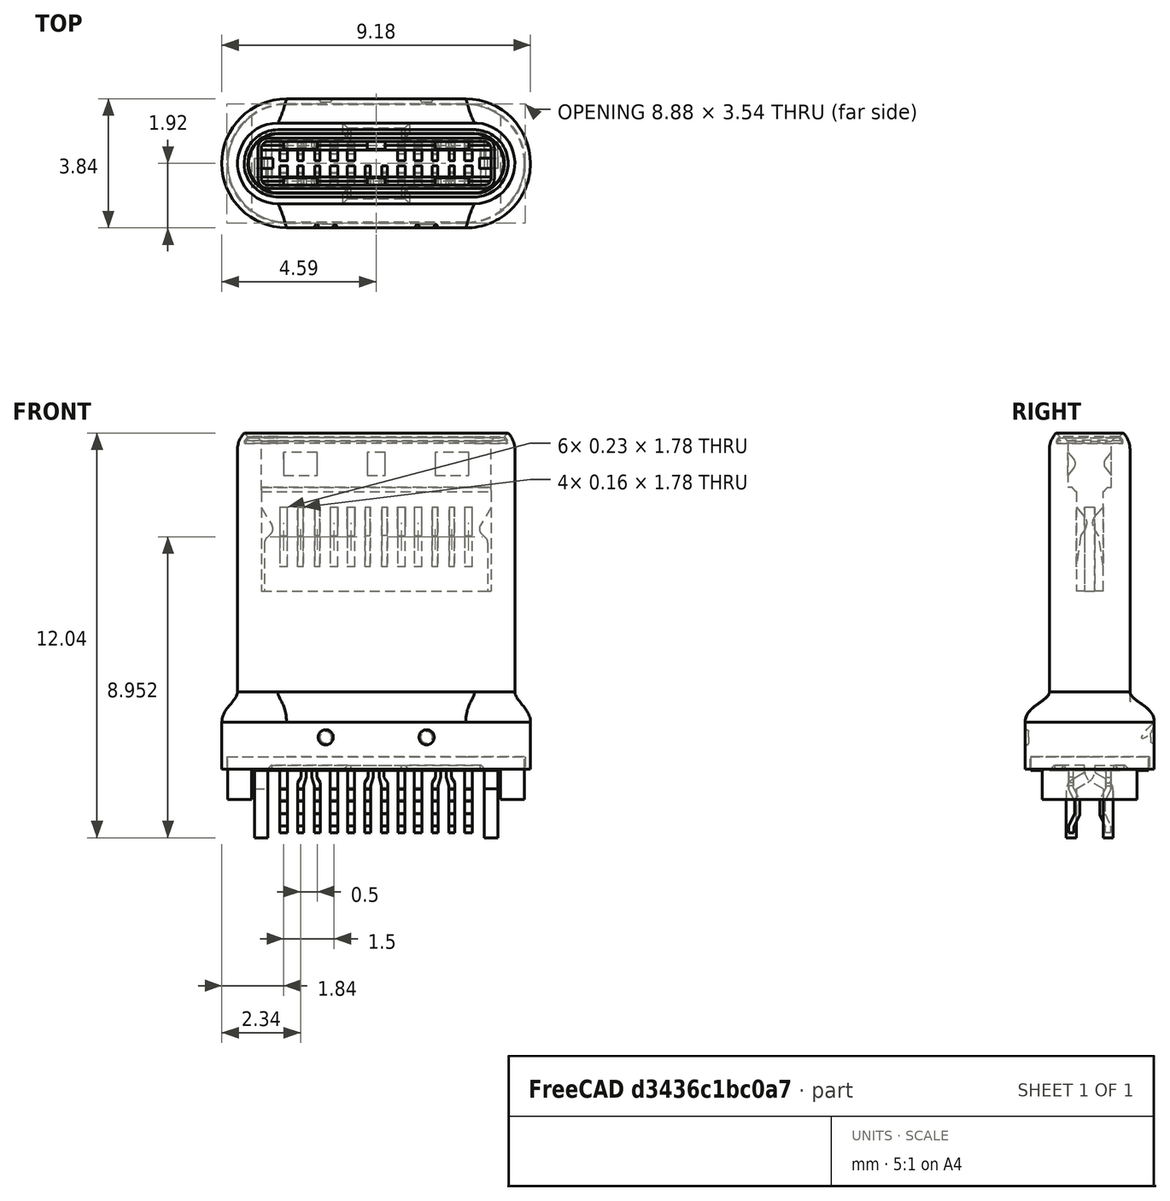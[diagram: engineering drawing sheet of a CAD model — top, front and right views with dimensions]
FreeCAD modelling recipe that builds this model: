
FCSTD DOCUMENT  (FreeCAD 0.16R6712 (Git))
Label: edges
License: All rights reserved
LicenseURL: http://en.wikipedia.org/wiki/All_rights_reserved
objects: Part::Feature×2, Sketcher::SketchObject×1
note: 3 computed .brp shape members not serialized (recipe doc carries the construction recipe); baked Part::Feature solids carry a one-line shape summary decoded from their .brp

FEATURE [Part::Feature] Part__Feature  label="SOLID"
  shape: bbox 9.212 x 3.852 x 12.05 mm, 648 faces (baked)
FEATURE [Part::Feature] Part__Feature001  label="COMPOUND"
  shape: bbox 7.54 x 0.6 x 1.955 mm, 0 faces, 0 solids (baked)
FEATURE [Sketcher::SketchObject] Sketch
  Placement = pos=(0,0,0) rot=(1,0,0;1.5708rad)
  sketch-geometry (15):
    g0: LineSegment StartX=-4.3 StartY=-7 StartZ=0 EndX=-4.3 EndY=-3.32 EndZ=0
    g1: LineSegment StartX=-4.3 StartY=-3.32 StartZ=0 EndX=-3.3 EndY=-3.32 EndZ=0
    g2: LineSegment StartX=-3.05 StartY=-3.07 StartZ=0 EndX=-3.05 EndY=-2.36 EndZ=0
    g3: LineSegment StartX=-3.05 StartY=-2.36 StartZ=0 EndX=3.05 EndY=-2.36 EndZ=0
    g4: LineSegment StartX=3.05 StartY=-2.36 StartZ=0 EndX=3.05 EndY=-3.07 EndZ=0
    g5: LineSegment StartX=3.3 StartY=-3.32 StartZ=0 EndX=4.3 EndY=-3.32 EndZ=0
    g6: LineSegment StartX=4.3 StartY=-3.32 StartZ=0 EndX=4.3 EndY=-7 EndZ=0
    g7: LineSegment StartX=4.3 StartY=-7 StartZ=0 EndX=-4.3 EndY=-7 EndZ=0
    g8: LineSegment StartX=-3.76988 StartY=-3.625 StartZ=0 EndX=-3.06988 EndY=-3.625 EndZ=0
    g9: LineSegment StartX=-3.06988 StartY=-3.625 StartZ=0 EndX=-3.06988 EndY=-4.775 EndZ=0
    g10: LineSegment StartX=-3.06988 StartY=-4.775 StartZ=0 EndX=-3.76988 EndY=-4.775 EndZ=0
    g11: LineSegment StartX=-3.76988 StartY=-4.775 StartZ=0 EndX=-3.76988 EndY=-3.625 EndZ=0
    g12: LineSegment [constr] StartX=-3.76988 StartY=-4.2 StartZ=0 EndX=-3.06988 EndY=-4.2 EndZ=0
    g13: ArcOfCircle CenterX=-3.3 CenterY=-3.07 CenterZ=0 NormalX=0 NormalY=0 NormalZ=1 Radius=0.25 StartAngle=4.71239 EndAngle=6.28319
    g14: ArcOfCircle CenterX=3.3 CenterY=-3.07 CenterZ=0 NormalX=0 NormalY=0 NormalZ=1 Radius=0.25 StartAngle=3.14159 EndAngle=4.71239
  constraints (44):
    c: Vertical(g0)
    c: Coincident(g0,g1)
    c: Horizontal(g1)
    c: Vertical(g2)
    c: Coincident(g2,g3)
    c: Horizontal(g3)
    c: Coincident(g3,g4)
    c: Vertical(g4)
    c: Horizontal(g5)
    c: Coincident(g5,g6)
    c: Vertical(g6)
    c: Coincident(g6,g7)
    c: Coincident(g7,g0)
    c: Horizontal(g7)
    c: Symmetric(g0,g6,g-2)
    c: DistanceX(g7,g7) = 8.6
    c: DistanceY(g0) = -7
    c: Coincident(g8,g9)
    c: Coincident(g9,g10)
    c: Coincident(g10,g11)
    c: Coincident(g11,g8)
    c: Horizontal(g8)
    c: Horizontal(g10)
    c: Vertical(g9)
    c: Vertical(g11)
    c: PointOnObject(g12,g11)
    c: PointOnObject(g12,g9)
    c: Horizontal(g12)
    c: Symmetric(g10,g8,g12)
    c: DistanceX(g12) = -3.76988
    c: DistanceY(g12) = -4.2
    c: DistanceY(g12,g2) = 1.84
    c: DistanceX(g10,g10) = 0.7
    c: DistanceY(g11,g11) = 1.15
    c: Tangent(g1,g13) = -1.5708
    c: Tangent(g2,g13) = -1.5708
    c: Tangent(g4,g14) = -1.5708
    c: Tangent(g5,g14) = -1.5708
    c: Radius(g14) = 0.25
    c: Equal(g14,g13)
    c: Symmetric(g2,g3,g-2)
    c: DistanceX(g3,g3) = 6.1
    c: DistanceY(g0,g2) = 0.96
    c: Equal(g0,g6)
